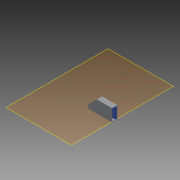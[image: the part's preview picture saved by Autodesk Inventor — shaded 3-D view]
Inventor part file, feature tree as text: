
AUTODESK INVENTOR PART (.ipt)
format: ipt  version: 2013 SP2 (Build 170200200, 200)  size: 109,056 bytes
history: native  units: mm
features: extrude x3, sketch x3, plane x1, chamfer x1
ambient origin geometry x8: Origin, YZ Plane, XZ Plane, XY Plane, X Axis, Y Axis, Z Axis, Center Point
bodies: Solid1 (feature_tree)
feature tree (8):
  plane  "Work Plane1"
  extrude  "Extrusion1"  Depth=5.8mm
  chamfer  "Chamfer1"  Distance=13.2mm
  extrude  "Extrusion2"  Depth=0.4mm
  extrude  "Extrusion3"  Depth=0.4mm
  sketch  "Sketch1"  dims[d0=25.7mm d2=5.8mm d3=13.2mm d4=0.0mm]
  sketch  "Sketch2"  dims[d5=9.2mm d6=2.0mm d7=45.0deg d8=0.4mm]
  sketch  "Sketch3"  dims[d9=16.0mm d10=0.0mm d11=0.4mm d12=0.4mm d13=0.4mm d14=1.4mm d15=16.0mm d16=0.0mm]
